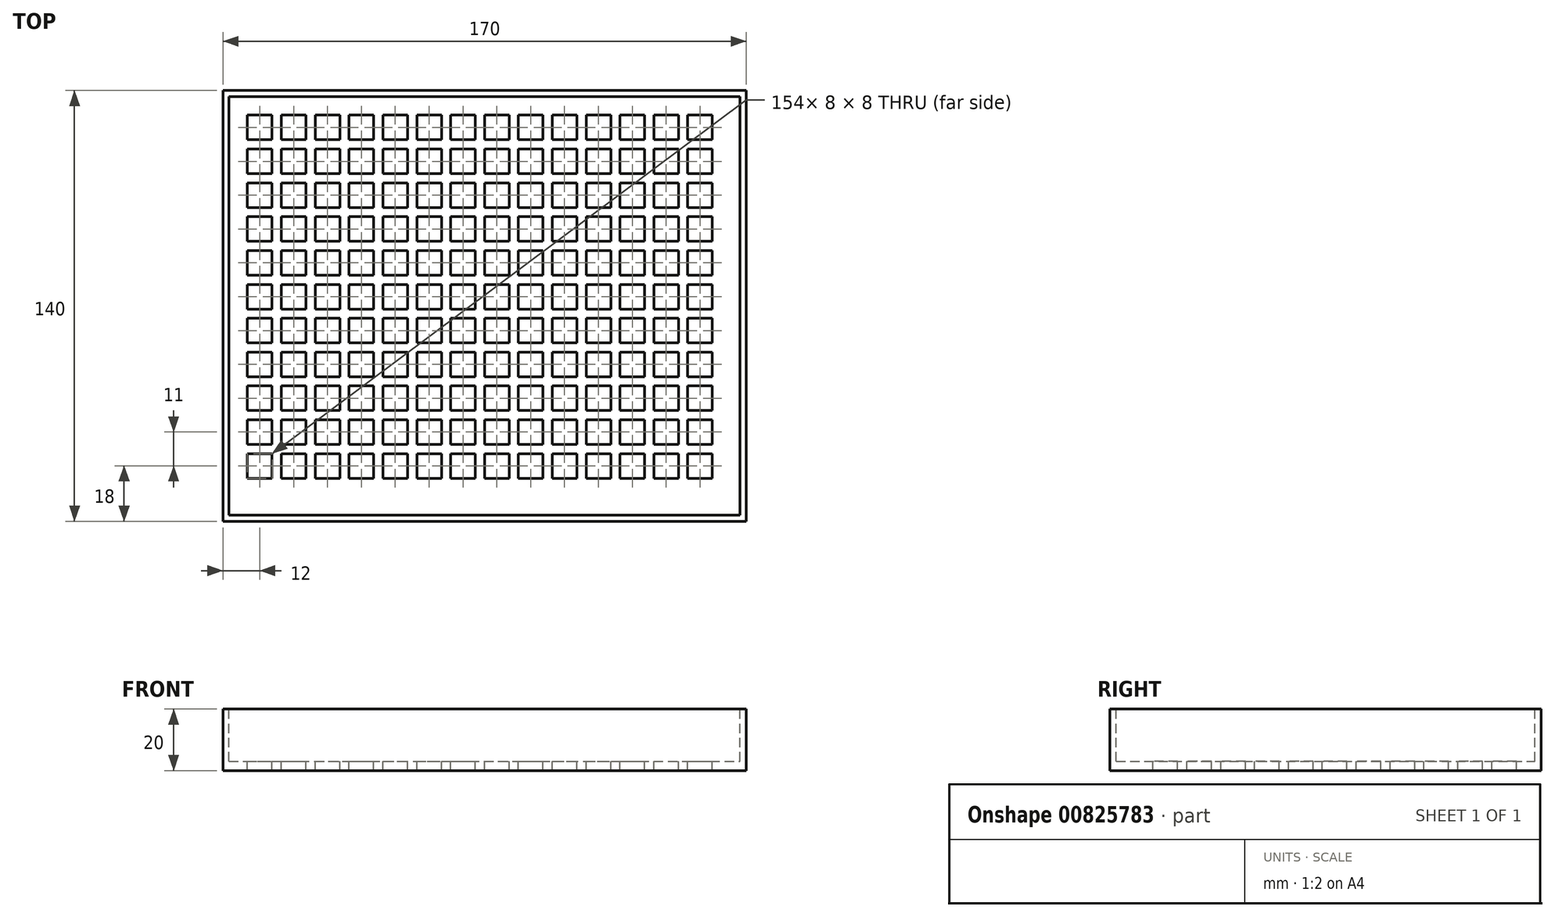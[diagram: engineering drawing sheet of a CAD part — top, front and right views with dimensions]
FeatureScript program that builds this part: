
annotation { "Feature Type Name" : "Feature", "Feature Type Description" : "" }
export const myFeature = defineFeature(function(context is Context, id is Id, definition is map)
    precondition{}
    {
        {
            var Q0;
            Q0=qCreatedBy(makeId("Top.planeOp"),FACE);
            var sketch = newSketch(context, id + "F0", { "sketchPlane" : qUnion([Q0])});
            skLineSegment(sketch, "E0.bottom", {"start": v(-85, 70) * mm, "end": v(85, 70) * mm});
            skLineSegment(sketch, "E0.top", {"start": v(-85, -70) * mm, "end": v(85, -70) * mm});
            skLineSegment(sketch, "E0.left", {"start": v(-85, 70) * mm, "end": v(-85, -70) * mm});
            skLineSegment(sketch, "E0.right", {"start": v(85, 70) * mm, "end": v(85, -70) * mm});
            skLineSegment(sketch, "E1", {"start": v(-85, 70) * mm, "end": v(85, -70) * mm, "construction": true});
            skLineSegment(sketch, "E2", {"start": v(85, 70) * mm, "end": v(-85, -70) * mm, "construction": true});
            skPoint(sketch, "E3", {"position": v(0, 0) * mm});
            skSolve(sketch);
        }
        {
            var Q0;
            Q0 = qSketchRegion(id + "F0", true);
            extrude(context, id + "F1", {"entities" : qUnion([Q0]), "depth" : 20 * mm, "offsetDistance" : 25 * mm});
        }
        {
            var Q0;
            Q0=makeQuery(id+"F1.opExtrude","CAP_FACE",FACE,{"disambiguationData":[OSD([sQuery(id+"F0.wireOp",EDGE,"E0.bottom"),sQuery(id+"F0.wireOp",EDGE,"E0.top"),sQuery(id+"F0.wireOp",EDGE,"E0.left"),sQuery(id+"F0.wireOp",EDGE,"E0.right")])],"isStart":false});
            var sketch = newSketch(context, id + "F2", { "sketchPlane" : qUnion([Q0])});
            skLineSegment(sketch, "E4.bottom", {"start": v(-77, 68) * mm, "end": v(77, 68) * mm});
            skLineSegment(sketch, "E4.top", {"start": v(-77, -68) * mm, "end": v(77, -68) * mm});
            skLineSegment(sketch, "E4.left", {"start": v(-83, 62) * mm, "end": v(-83, -62) * mm});
            skLineSegment(sketch, "E4.right", {"start": v(83, 62) * mm, "end": v(83, -62) * mm});
            skPoint(sketch, "E5.visualSharp", {"position": v(-83, 68) * mm});
            skPoint(sketch, "E6.visualSharp", {"position": v(-83, -68) * mm});
            skPoint(sketch, "E7.visualSharp", {"position": v(83, 68) * mm});
            skPoint(sketch, "E8.visualSharp", {"position": v(83, -68) * mm});
            skLineSegment(sketch, "E9", {"start": v(-83, 62) * mm, "end": v(-83, 68) * mm});
            skLineSegment(sketch, "E10", {"start": v(-83, 68) * mm, "end": v(-77, 68) * mm});
            skLineSegment(sketch, "E11", {"start": v(77, 68) * mm, "end": v(83, 68) * mm});
            skLineSegment(sketch, "E12", {"start": v(83, 62) * mm, "end": v(83, 68) * mm});
            skLineSegment(sketch, "E13", {"start": v(77, -68) * mm, "end": v(83, -68) * mm});
            skLineSegment(sketch, "E14", {"start": v(83, -62) * mm, "end": v(83, -68) * mm});
            skLineSegment(sketch, "E15", {"start": v(-77, -68) * mm, "end": v(-83, -68) * mm});
            skLineSegment(sketch, "E16", {"start": v(-83, -62) * mm, "end": v(-83, -68) * mm});
            skSolve(sketch);
        }
        {
            var Q0;
            Q0 = qSketchRegion(id + "F2", true);
            extrude(context, id + "F3", {"entities" : qUnion([Q0]), "operationType" : NewBodyOperationType.REMOVE, "oppositeDirection" : true, "depth" : 17 * mm, "offsetDistance" : 25 * mm});
        }
        {
            var Q0;
            Q0=makeQuery(id+"F3.boolean.opBoolean","COPY",FACE,{"derivedFrom":makeQuery(id+"F3.opExtrude","CAP_FACE",FACE,{"disambiguationData":[OSD([sQuery(id+"F2.wireOp",EDGE,"E4.bottom"),sQuery(id+"F2.wireOp",EDGE,"E4.top"),sQuery(id+"F2.wireOp",EDGE,"E4.left"),sQuery(id+"F2.wireOp",EDGE,"E4.right"),sQuery(id+"F2.wireOp",EDGE,"E5.filletArc"),sQuery(id+"F2.wireOp",EDGE,"E6.filletArc"),sQuery(id+"F2.wireOp",EDGE,"E7.filletArc"),sQuery(id+"F2.wireOp",EDGE,"E8.filletArc")])],"isStart":false})});
            var sketch = newSketch(context, id + "F4", { "sketchPlane" : qUnion([Q0])});
            skLineSegment(sketch, "E17.bottom", {"start": v(-77, 62) * mm, "end": v(-69, 62) * mm});
            skLineSegment(sketch, "E17.top", {"start": v(-77, 54) * mm, "end": v(-69, 54) * mm});
            skLineSegment(sketch, "E17.left", {"start": v(-77, 62) * mm, "end": v(-77, 54) * mm});
            skLineSegment(sketch, "E17.right", {"start": v(-69, 62) * mm, "end": v(-69, 54) * mm});
            skLineSegment(sketch, "E18.0.1.0", {"start": v(-69, 51) * mm, "end": v(-69, 43) * mm});
            skLineSegment(sketch, "E18.0.1.1", {"start": v(-77, 51) * mm, "end": v(-69, 51) * mm});
            skLineSegment(sketch, "E18.0.1.2", {"start": v(-77, 43) * mm, "end": v(-69, 43) * mm});
            skLineSegment(sketch, "E18.0.1.3", {"start": v(-77, 51) * mm, "end": v(-77, 43) * mm});
            skLineSegment(sketch, "E18.0.2.0", {"start": v(-69, 40) * mm, "end": v(-69, 32) * mm});
            skLineSegment(sketch, "E18.0.2.1", {"start": v(-77, 40) * mm, "end": v(-69, 40) * mm});
            skLineSegment(sketch, "E18.0.2.2", {"start": v(-77, 32) * mm, "end": v(-69, 32) * mm});
            skLineSegment(sketch, "E18.0.2.3", {"start": v(-77, 40) * mm, "end": v(-77, 32) * mm});
            skLineSegment(sketch, "E18.0.3.0", {"start": v(-69, 29) * mm, "end": v(-69, 21) * mm});
            skLineSegment(sketch, "E18.0.3.1", {"start": v(-77, 29) * mm, "end": v(-69, 29) * mm});
            skLineSegment(sketch, "E18.0.3.2", {"start": v(-77, 21) * mm, "end": v(-69, 21) * mm});
            skLineSegment(sketch, "E18.0.3.3", {"start": v(-77, 29) * mm, "end": v(-77, 21) * mm});
            skLineSegment(sketch, "E18.0.4.0", {"start": v(-69, 18) * mm, "end": v(-69, 10) * mm});
            skLineSegment(sketch, "E18.0.4.1", {"start": v(-77, 18) * mm, "end": v(-69, 18) * mm});
            skLineSegment(sketch, "E18.0.4.2", {"start": v(-77, 10) * mm, "end": v(-69, 10) * mm});
            skLineSegment(sketch, "E18.0.4.3", {"start": v(-77, 18) * mm, "end": v(-77, 10) * mm});
            skLineSegment(sketch, "E18.0.5.0", {"start": v(-69, 7) * mm, "end": v(-69, -1) * mm});
            skLineSegment(sketch, "E18.0.5.1", {"start": v(-77, 7) * mm, "end": v(-69, 7) * mm});
            skLineSegment(sketch, "E18.0.5.2", {"start": v(-77, -1) * mm, "end": v(-69, -1) * mm});
            skLineSegment(sketch, "E18.0.5.3", {"start": v(-77, 7) * mm, "end": v(-77, -1) * mm});
            skLineSegment(sketch, "E18.0.6.0", {"start": v(-69, -4) * mm, "end": v(-69, -12) * mm});
            skLineSegment(sketch, "E18.0.6.1", {"start": v(-77, -4) * mm, "end": v(-69, -4) * mm});
            skLineSegment(sketch, "E18.0.6.2", {"start": v(-77, -12) * mm, "end": v(-69, -12) * mm});
            skLineSegment(sketch, "E18.0.6.3", {"start": v(-77, -4) * mm, "end": v(-77, -12) * mm});
            skLineSegment(sketch, "E18.0.7.0", {"start": v(-69, -15) * mm, "end": v(-69, -23) * mm});
            skLineSegment(sketch, "E18.0.7.1", {"start": v(-77, -15) * mm, "end": v(-69, -15) * mm});
            skLineSegment(sketch, "E18.0.7.2", {"start": v(-77, -23) * mm, "end": v(-69, -23) * mm});
            skLineSegment(sketch, "E18.0.7.3", {"start": v(-77, -15) * mm, "end": v(-77, -23) * mm});
            skLineSegment(sketch, "E18.0.8.0", {"start": v(-69, -26) * mm, "end": v(-69, -34) * mm});
            skLineSegment(sketch, "E18.0.8.1", {"start": v(-77, -26) * mm, "end": v(-69, -26) * mm});
            skLineSegment(sketch, "E18.0.8.2", {"start": v(-77, -34) * mm, "end": v(-69, -34) * mm});
            skLineSegment(sketch, "E18.0.8.3", {"start": v(-77, -26) * mm, "end": v(-77, -34) * mm});
            skLineSegment(sketch, "E18.0.9.0", {"start": v(-69, -37) * mm, "end": v(-69, -45) * mm});
            skLineSegment(sketch, "E18.0.9.1", {"start": v(-77, -37) * mm, "end": v(-69, -37) * mm});
            skLineSegment(sketch, "E18.0.9.2", {"start": v(-77, -45) * mm, "end": v(-69, -45) * mm});
            skLineSegment(sketch, "E18.0.9.3", {"start": v(-77, -37) * mm, "end": v(-77, -45) * mm});
            skLineSegment(sketch, "E18.0.10.0", {"start": v(-69, -48) * mm, "end": v(-69, -56) * mm});
            skLineSegment(sketch, "E18.0.10.1", {"start": v(-77, -48) * mm, "end": v(-69, -48) * mm});
            skLineSegment(sketch, "E18.0.10.2", {"start": v(-77, -56) * mm, "end": v(-69, -56) * mm});
            skLineSegment(sketch, "E18.0.10.3", {"start": v(-77, -48) * mm, "end": v(-77, -56) * mm});
            skLineSegment(sketch, "E18.1.0.0", {"start": v(-58, 62) * mm, "end": v(-58, 54) * mm});
            skLineSegment(sketch, "E18.1.0.1", {"start": v(-66, 62) * mm, "end": v(-58, 62) * mm});
            skLineSegment(sketch, "E18.1.0.2", {"start": v(-66, 54) * mm, "end": v(-58, 54) * mm});
            skLineSegment(sketch, "E18.1.0.3", {"start": v(-66, 62) * mm, "end": v(-66, 54) * mm});
            skLineSegment(sketch, "E18.1.1.0", {"start": v(-58, 51) * mm, "end": v(-58, 43) * mm});
            skLineSegment(sketch, "E18.1.1.1", {"start": v(-66, 51) * mm, "end": v(-58, 51) * mm});
            skLineSegment(sketch, "E18.1.1.2", {"start": v(-66, 43) * mm, "end": v(-58, 43) * mm});
            skLineSegment(sketch, "E18.1.1.3", {"start": v(-66, 51) * mm, "end": v(-66, 43) * mm});
            skLineSegment(sketch, "E18.1.2.0", {"start": v(-58, 40) * mm, "end": v(-58, 32) * mm});
            skLineSegment(sketch, "E18.1.2.1", {"start": v(-66, 40) * mm, "end": v(-58, 40) * mm});
            skLineSegment(sketch, "E18.1.2.2", {"start": v(-66, 32) * mm, "end": v(-58, 32) * mm});
            skLineSegment(sketch, "E18.1.2.3", {"start": v(-66, 40) * mm, "end": v(-66, 32) * mm});
            skLineSegment(sketch, "E18.1.3.0", {"start": v(-58, 29) * mm, "end": v(-58, 21) * mm});
            skLineSegment(sketch, "E18.1.3.1", {"start": v(-66, 29) * mm, "end": v(-58, 29) * mm});
            skLineSegment(sketch, "E18.1.3.2", {"start": v(-66, 21) * mm, "end": v(-58, 21) * mm});
            skLineSegment(sketch, "E18.1.3.3", {"start": v(-66, 29) * mm, "end": v(-66, 21) * mm});
            skLineSegment(sketch, "E18.1.4.0", {"start": v(-58, 18) * mm, "end": v(-58, 10) * mm});
            skLineSegment(sketch, "E18.1.4.1", {"start": v(-66, 18) * mm, "end": v(-58, 18) * mm});
            skLineSegment(sketch, "E18.1.4.2", {"start": v(-66, 10) * mm, "end": v(-58, 10) * mm});
            skLineSegment(sketch, "E18.1.4.3", {"start": v(-66, 18) * mm, "end": v(-66, 10) * mm});
            skLineSegment(sketch, "E18.1.5.0", {"start": v(-58, 7) * mm, "end": v(-58, -1) * mm});
            skLineSegment(sketch, "E18.1.5.1", {"start": v(-66, 7) * mm, "end": v(-58, 7) * mm});
            skLineSegment(sketch, "E18.1.5.2", {"start": v(-66, -1) * mm, "end": v(-58, -1) * mm});
            skLineSegment(sketch, "E18.1.5.3", {"start": v(-66, 7) * mm, "end": v(-66, -1) * mm});
            skLineSegment(sketch, "E18.1.6.0", {"start": v(-58, -4) * mm, "end": v(-58, -12) * mm});
            skLineSegment(sketch, "E18.1.6.1", {"start": v(-66, -4) * mm, "end": v(-58, -4) * mm});
            skLineSegment(sketch, "E18.1.6.2", {"start": v(-66, -12) * mm, "end": v(-58, -12) * mm});
            skLineSegment(sketch, "E18.1.6.3", {"start": v(-66, -4) * mm, "end": v(-66, -12) * mm});
            skLineSegment(sketch, "E18.1.7.0", {"start": v(-58, -15) * mm, "end": v(-58, -23) * mm});
            skLineSegment(sketch, "E18.1.7.1", {"start": v(-66, -15) * mm, "end": v(-58, -15) * mm});
            skLineSegment(sketch, "E18.1.7.2", {"start": v(-66, -23) * mm, "end": v(-58, -23) * mm});
            skLineSegment(sketch, "E18.1.7.3", {"start": v(-66, -15) * mm, "end": v(-66, -23) * mm});
            skLineSegment(sketch, "E18.1.8.0", {"start": v(-58, -26) * mm, "end": v(-58, -34) * mm});
            skLineSegment(sketch, "E18.1.8.1", {"start": v(-66, -26) * mm, "end": v(-58, -26) * mm});
            skLineSegment(sketch, "E18.1.8.2", {"start": v(-66, -34) * mm, "end": v(-58, -34) * mm});
            skLineSegment(sketch, "E18.1.8.3", {"start": v(-66, -26) * mm, "end": v(-66, -34) * mm});
            skLineSegment(sketch, "E18.1.9.0", {"start": v(-58, -37) * mm, "end": v(-58, -45) * mm});
            skLineSegment(sketch, "E18.1.9.1", {"start": v(-66, -37) * mm, "end": v(-58, -37) * mm});
            skLineSegment(sketch, "E18.1.9.2", {"start": v(-66, -45) * mm, "end": v(-58, -45) * mm});
            skLineSegment(sketch, "E18.1.9.3", {"start": v(-66, -37) * mm, "end": v(-66, -45) * mm});
            skLineSegment(sketch, "E18.1.10.0", {"start": v(-58, -48) * mm, "end": v(-58, -56) * mm});
            skLineSegment(sketch, "E18.1.10.1", {"start": v(-66, -48) * mm, "end": v(-58, -48) * mm});
            skLineSegment(sketch, "E18.1.10.2", {"start": v(-66, -56) * mm, "end": v(-58, -56) * mm});
            skLineSegment(sketch, "E18.1.10.3", {"start": v(-66, -48) * mm, "end": v(-66, -56) * mm});
            skLineSegment(sketch, "E18.2.0.0", {"start": v(-47, 62) * mm, "end": v(-47, 54) * mm});
            skLineSegment(sketch, "E18.2.0.1", {"start": v(-55, 62) * mm, "end": v(-47, 62) * mm});
            skLineSegment(sketch, "E18.2.0.2", {"start": v(-55, 54) * mm, "end": v(-47, 54) * mm});
            skLineSegment(sketch, "E18.2.0.3", {"start": v(-55, 62) * mm, "end": v(-55, 54) * mm});
            skLineSegment(sketch, "E18.2.1.0", {"start": v(-47, 51) * mm, "end": v(-47, 43) * mm});
            skLineSegment(sketch, "E18.2.1.1", {"start": v(-55, 51) * mm, "end": v(-47, 51) * mm});
            skLineSegment(sketch, "E18.2.1.2", {"start": v(-55, 43) * mm, "end": v(-47, 43) * mm});
            skLineSegment(sketch, "E18.2.1.3", {"start": v(-55, 51) * mm, "end": v(-55, 43) * mm});
            skLineSegment(sketch, "E18.2.2.0", {"start": v(-47, 40) * mm, "end": v(-47, 32) * mm});
            skLineSegment(sketch, "E18.2.2.1", {"start": v(-55, 40) * mm, "end": v(-47, 40) * mm});
            skLineSegment(sketch, "E18.2.2.2", {"start": v(-55, 32) * mm, "end": v(-47, 32) * mm});
            skLineSegment(sketch, "E18.2.2.3", {"start": v(-55, 40) * mm, "end": v(-55, 32) * mm});
            skLineSegment(sketch, "E18.2.3.0", {"start": v(-47, 29) * mm, "end": v(-47, 21) * mm});
            skLineSegment(sketch, "E18.2.3.1", {"start": v(-55, 29) * mm, "end": v(-47, 29) * mm});
            skLineSegment(sketch, "E18.2.3.2", {"start": v(-55, 21) * mm, "end": v(-47, 21) * mm});
            skLineSegment(sketch, "E18.2.3.3", {"start": v(-55, 29) * mm, "end": v(-55, 21) * mm});
            skLineSegment(sketch, "E18.2.4.0", {"start": v(-47, 18) * mm, "end": v(-47, 10) * mm});
            skLineSegment(sketch, "E18.2.4.1", {"start": v(-55, 18) * mm, "end": v(-47, 18) * mm});
            skLineSegment(sketch, "E18.2.4.2", {"start": v(-55, 10) * mm, "end": v(-47, 10) * mm});
            skLineSegment(sketch, "E18.2.4.3", {"start": v(-55, 18) * mm, "end": v(-55, 10) * mm});
            skLineSegment(sketch, "E18.2.5.0", {"start": v(-47, 7) * mm, "end": v(-47, -1) * mm});
            skLineSegment(sketch, "E18.2.5.1", {"start": v(-55, 7) * mm, "end": v(-47, 7) * mm});
            skLineSegment(sketch, "E18.2.5.2", {"start": v(-55, -1) * mm, "end": v(-47, -1) * mm});
            skLineSegment(sketch, "E18.2.5.3", {"start": v(-55, 7) * mm, "end": v(-55, -1) * mm});
            skLineSegment(sketch, "E18.2.6.0", {"start": v(-47, -4) * mm, "end": v(-47, -12) * mm});
            skLineSegment(sketch, "E18.2.6.1", {"start": v(-55, -4) * mm, "end": v(-47, -4) * mm});
            skLineSegment(sketch, "E18.2.6.2", {"start": v(-55, -12) * mm, "end": v(-47, -12) * mm});
            skLineSegment(sketch, "E18.2.6.3", {"start": v(-55, -4) * mm, "end": v(-55, -12) * mm});
            skLineSegment(sketch, "E18.2.7.0", {"start": v(-47, -15) * mm, "end": v(-47, -23) * mm});
            skLineSegment(sketch, "E18.2.7.1", {"start": v(-55, -15) * mm, "end": v(-47, -15) * mm});
            skLineSegment(sketch, "E18.2.7.2", {"start": v(-55, -23) * mm, "end": v(-47, -23) * mm});
            skLineSegment(sketch, "E18.2.7.3", {"start": v(-55, -15) * mm, "end": v(-55, -23) * mm});
            skLineSegment(sketch, "E18.2.8.0", {"start": v(-47, -26) * mm, "end": v(-47, -34) * mm});
            skLineSegment(sketch, "E18.2.8.1", {"start": v(-55, -26) * mm, "end": v(-47, -26) * mm});
            skLineSegment(sketch, "E18.2.8.2", {"start": v(-55, -34) * mm, "end": v(-47, -34) * mm});
            skLineSegment(sketch, "E18.2.8.3", {"start": v(-55, -26) * mm, "end": v(-55, -34) * mm});
            skLineSegment(sketch, "E18.2.9.0", {"start": v(-47, -37) * mm, "end": v(-47, -45) * mm});
            skLineSegment(sketch, "E18.2.9.1", {"start": v(-55, -37) * mm, "end": v(-47, -37) * mm});
            skLineSegment(sketch, "E18.2.9.2", {"start": v(-55, -45) * mm, "end": v(-47, -45) * mm});
            skLineSegment(sketch, "E18.2.9.3", {"start": v(-55, -37) * mm, "end": v(-55, -45) * mm});
            skLineSegment(sketch, "E18.2.10.0", {"start": v(-47, -48) * mm, "end": v(-47, -56) * mm});
            skLineSegment(sketch, "E18.2.10.1", {"start": v(-55, -48) * mm, "end": v(-47, -48) * mm});
            skLineSegment(sketch, "E18.2.10.2", {"start": v(-55, -56) * mm, "end": v(-47, -56) * mm});
            skLineSegment(sketch, "E18.2.10.3", {"start": v(-55, -48) * mm, "end": v(-55, -56) * mm});
            skLineSegment(sketch, "E18.3.0.0", {"start": v(-36, 62) * mm, "end": v(-36, 54) * mm});
            skLineSegment(sketch, "E18.3.0.1", {"start": v(-44, 62) * mm, "end": v(-36, 62) * mm});
            skLineSegment(sketch, "E18.3.0.2", {"start": v(-44, 54) * mm, "end": v(-36, 54) * mm});
            skLineSegment(sketch, "E18.3.0.3", {"start": v(-44, 62) * mm, "end": v(-44, 54) * mm});
            skLineSegment(sketch, "E18.3.1.0", {"start": v(-36, 51) * mm, "end": v(-36, 43) * mm});
            skLineSegment(sketch, "E18.3.1.1", {"start": v(-44, 51) * mm, "end": v(-36, 51) * mm});
            skLineSegment(sketch, "E18.3.1.2", {"start": v(-44, 43) * mm, "end": v(-36, 43) * mm});
            skLineSegment(sketch, "E18.3.1.3", {"start": v(-44, 51) * mm, "end": v(-44, 43) * mm});
            skLineSegment(sketch, "E18.3.2.0", {"start": v(-36, 40) * mm, "end": v(-36, 32) * mm});
            skLineSegment(sketch, "E18.3.2.1", {"start": v(-44, 40) * mm, "end": v(-36, 40) * mm});
            skLineSegment(sketch, "E18.3.2.2", {"start": v(-44, 32) * mm, "end": v(-36, 32) * mm});
            skLineSegment(sketch, "E18.3.2.3", {"start": v(-44, 40) * mm, "end": v(-44, 32) * mm});
            skLineSegment(sketch, "E18.3.3.0", {"start": v(-36, 29) * mm, "end": v(-36, 21) * mm});
            skLineSegment(sketch, "E18.3.3.1", {"start": v(-44, 29) * mm, "end": v(-36, 29) * mm});
            skLineSegment(sketch, "E18.3.3.2", {"start": v(-44, 21) * mm, "end": v(-36, 21) * mm});
            skLineSegment(sketch, "E18.3.3.3", {"start": v(-44, 29) * mm, "end": v(-44, 21) * mm});
            skLineSegment(sketch, "E18.3.4.0", {"start": v(-36, 18) * mm, "end": v(-36, 10) * mm});
            skLineSegment(sketch, "E18.3.4.1", {"start": v(-44, 18) * mm, "end": v(-36, 18) * mm});
            skLineSegment(sketch, "E18.3.4.2", {"start": v(-44, 10) * mm, "end": v(-36, 10) * mm});
            skLineSegment(sketch, "E18.3.4.3", {"start": v(-44, 18) * mm, "end": v(-44, 10) * mm});
            skLineSegment(sketch, "E18.3.5.0", {"start": v(-36, 7) * mm, "end": v(-36, -1) * mm});
            skLineSegment(sketch, "E18.3.5.1", {"start": v(-44, 7) * mm, "end": v(-36, 7) * mm});
            skLineSegment(sketch, "E18.3.5.2", {"start": v(-44, -1) * mm, "end": v(-36, -1) * mm});
            skLineSegment(sketch, "E18.3.5.3", {"start": v(-44, 7) * mm, "end": v(-44, -1) * mm});
            skLineSegment(sketch, "E18.3.6.0", {"start": v(-36, -4) * mm, "end": v(-36, -12) * mm});
            skLineSegment(sketch, "E18.3.6.1", {"start": v(-44, -4) * mm, "end": v(-36, -4) * mm});
            skLineSegment(sketch, "E18.3.6.2", {"start": v(-44, -12) * mm, "end": v(-36, -12) * mm});
            skLineSegment(sketch, "E18.3.6.3", {"start": v(-44, -4) * mm, "end": v(-44, -12) * mm});
            skLineSegment(sketch, "E18.3.7.0", {"start": v(-36, -15) * mm, "end": v(-36, -23) * mm});
            skLineSegment(sketch, "E18.3.7.1", {"start": v(-44, -15) * mm, "end": v(-36, -15) * mm});
            skLineSegment(sketch, "E18.3.7.2", {"start": v(-44, -23) * mm, "end": v(-36, -23) * mm});
            skLineSegment(sketch, "E18.3.7.3", {"start": v(-44, -15) * mm, "end": v(-44, -23) * mm});
            skLineSegment(sketch, "E18.3.8.0", {"start": v(-36, -26) * mm, "end": v(-36, -34) * mm});
            skLineSegment(sketch, "E18.3.8.1", {"start": v(-44, -26) * mm, "end": v(-36, -26) * mm});
            skLineSegment(sketch, "E18.3.8.2", {"start": v(-44, -34) * mm, "end": v(-36, -34) * mm});
            skLineSegment(sketch, "E18.3.8.3", {"start": v(-44, -26) * mm, "end": v(-44, -34) * mm});
            skLineSegment(sketch, "E18.3.9.0", {"start": v(-36, -37) * mm, "end": v(-36, -45) * mm});
            skLineSegment(sketch, "E18.3.9.1", {"start": v(-44, -37) * mm, "end": v(-36, -37) * mm});
            skLineSegment(sketch, "E18.3.9.2", {"start": v(-44, -45) * mm, "end": v(-36, -45) * mm});
            skLineSegment(sketch, "E18.3.9.3", {"start": v(-44, -37) * mm, "end": v(-44, -45) * mm});
            skLineSegment(sketch, "E18.3.10.0", {"start": v(-36, -48) * mm, "end": v(-36, -56) * mm});
            skLineSegment(sketch, "E18.3.10.1", {"start": v(-44, -48) * mm, "end": v(-36, -48) * mm});
            skLineSegment(sketch, "E18.3.10.2", {"start": v(-44, -56) * mm, "end": v(-36, -56) * mm});
            skLineSegment(sketch, "E18.3.10.3", {"start": v(-44, -48) * mm, "end": v(-44, -56) * mm});
            skLineSegment(sketch, "E18.4.0.0", {"start": v(-25, 62) * mm, "end": v(-25, 54) * mm});
            skLineSegment(sketch, "E18.4.0.1", {"start": v(-33, 62) * mm, "end": v(-25, 62) * mm});
            skLineSegment(sketch, "E18.4.0.2", {"start": v(-33, 54) * mm, "end": v(-25, 54) * mm});
            skLineSegment(sketch, "E18.4.0.3", {"start": v(-33, 62) * mm, "end": v(-33, 54) * mm});
            skLineSegment(sketch, "E18.4.1.0", {"start": v(-25, 51) * mm, "end": v(-25, 43) * mm});
            skLineSegment(sketch, "E18.4.1.1", {"start": v(-33, 51) * mm, "end": v(-25, 51) * mm});
            skLineSegment(sketch, "E18.4.1.2", {"start": v(-33, 43) * mm, "end": v(-25, 43) * mm});
            skLineSegment(sketch, "E18.4.1.3", {"start": v(-33, 51) * mm, "end": v(-33, 43) * mm});
            skLineSegment(sketch, "E18.4.2.0", {"start": v(-25, 40) * mm, "end": v(-25, 32) * mm});
            skLineSegment(sketch, "E18.4.2.1", {"start": v(-33, 40) * mm, "end": v(-25, 40) * mm});
            skLineSegment(sketch, "E18.4.2.2", {"start": v(-33, 32) * mm, "end": v(-25, 32) * mm});
            skLineSegment(sketch, "E18.4.2.3", {"start": v(-33, 40) * mm, "end": v(-33, 32) * mm});
            skLineSegment(sketch, "E18.4.3.0", {"start": v(-25, 29) * mm, "end": v(-25, 21) * mm});
            skLineSegment(sketch, "E18.4.3.1", {"start": v(-33, 29) * mm, "end": v(-25, 29) * mm});
            skLineSegment(sketch, "E18.4.3.2", {"start": v(-33, 21) * mm, "end": v(-25, 21) * mm});
            skLineSegment(sketch, "E18.4.3.3", {"start": v(-33, 29) * mm, "end": v(-33, 21) * mm});
            skLineSegment(sketch, "E18.4.4.0", {"start": v(-25, 18) * mm, "end": v(-25, 10) * mm});
            skLineSegment(sketch, "E18.4.4.1", {"start": v(-33, 18) * mm, "end": v(-25, 18) * mm});
            skLineSegment(sketch, "E18.4.4.2", {"start": v(-33, 10) * mm, "end": v(-25, 10) * mm});
            skLineSegment(sketch, "E18.4.4.3", {"start": v(-33, 18) * mm, "end": v(-33, 10) * mm});
            skLineSegment(sketch, "E18.4.5.0", {"start": v(-25, 7) * mm, "end": v(-25, -1) * mm});
            skLineSegment(sketch, "E18.4.5.1", {"start": v(-33, 7) * mm, "end": v(-25, 7) * mm});
            skLineSegment(sketch, "E18.4.5.2", {"start": v(-33, -1) * mm, "end": v(-25, -1) * mm});
            skLineSegment(sketch, "E18.4.5.3", {"start": v(-33, 7) * mm, "end": v(-33, -1) * mm});
            skLineSegment(sketch, "E18.4.6.0", {"start": v(-25, -4) * mm, "end": v(-25, -12) * mm});
            skLineSegment(sketch, "E18.4.6.1", {"start": v(-33, -4) * mm, "end": v(-25, -4) * mm});
            skLineSegment(sketch, "E18.4.6.2", {"start": v(-33, -12) * mm, "end": v(-25, -12) * mm});
            skLineSegment(sketch, "E18.4.6.3", {"start": v(-33, -4) * mm, "end": v(-33, -12) * mm});
            skLineSegment(sketch, "E18.4.7.0", {"start": v(-25, -15) * mm, "end": v(-25, -23) * mm});
            skLineSegment(sketch, "E18.4.7.1", {"start": v(-33, -15) * mm, "end": v(-25, -15) * mm});
            skLineSegment(sketch, "E18.4.7.2", {"start": v(-33, -23) * mm, "end": v(-25, -23) * mm});
            skLineSegment(sketch, "E18.4.7.3", {"start": v(-33, -15) * mm, "end": v(-33, -23) * mm});
            skLineSegment(sketch, "E18.4.8.0", {"start": v(-25, -26) * mm, "end": v(-25, -34) * mm});
            skLineSegment(sketch, "E18.4.8.1", {"start": v(-33, -26) * mm, "end": v(-25, -26) * mm});
            skLineSegment(sketch, "E18.4.8.2", {"start": v(-33, -34) * mm, "end": v(-25, -34) * mm});
            skLineSegment(sketch, "E18.4.8.3", {"start": v(-33, -26) * mm, "end": v(-33, -34) * mm});
            skLineSegment(sketch, "E18.4.9.0", {"start": v(-25, -37) * mm, "end": v(-25, -45) * mm});
            skLineSegment(sketch, "E18.4.9.1", {"start": v(-33, -37) * mm, "end": v(-25, -37) * mm});
            skLineSegment(sketch, "E18.4.9.2", {"start": v(-33, -45) * mm, "end": v(-25, -45) * mm});
            skLineSegment(sketch, "E18.4.9.3", {"start": v(-33, -37) * mm, "end": v(-33, -45) * mm});
            skLineSegment(sketch, "E18.4.10.0", {"start": v(-25, -48) * mm, "end": v(-25, -56) * mm});
            skLineSegment(sketch, "E18.4.10.1", {"start": v(-33, -48) * mm, "end": v(-25, -48) * mm});
            skLineSegment(sketch, "E18.4.10.2", {"start": v(-33, -56) * mm, "end": v(-25, -56) * mm});
            skLineSegment(sketch, "E18.4.10.3", {"start": v(-33, -48) * mm, "end": v(-33, -56) * mm});
            skLineSegment(sketch, "E18.5.0.0", {"start": v(-14, 62) * mm, "end": v(-14, 54) * mm});
            skLineSegment(sketch, "E18.5.0.1", {"start": v(-22, 62) * mm, "end": v(-14, 62) * mm});
            skLineSegment(sketch, "E18.5.0.2", {"start": v(-22, 54) * mm, "end": v(-14, 54) * mm});
            skLineSegment(sketch, "E18.5.0.3", {"start": v(-22, 62) * mm, "end": v(-22, 54) * mm});
            skLineSegment(sketch, "E18.5.1.0", {"start": v(-14, 51) * mm, "end": v(-14, 43) * mm});
            skLineSegment(sketch, "E18.5.1.1", {"start": v(-22, 51) * mm, "end": v(-14, 51) * mm});
            skLineSegment(sketch, "E18.5.1.2", {"start": v(-22, 43) * mm, "end": v(-14, 43) * mm});
            skLineSegment(sketch, "E18.5.1.3", {"start": v(-22, 51) * mm, "end": v(-22, 43) * mm});
            skLineSegment(sketch, "E18.5.2.0", {"start": v(-14, 40) * mm, "end": v(-14, 32) * mm});
            skLineSegment(sketch, "E18.5.2.1", {"start": v(-22, 40) * mm, "end": v(-14, 40) * mm});
            skLineSegment(sketch, "E18.5.2.2", {"start": v(-22, 32) * mm, "end": v(-14, 32) * mm});
            skLineSegment(sketch, "E18.5.2.3", {"start": v(-22, 40) * mm, "end": v(-22, 32) * mm});
            skLineSegment(sketch, "E18.5.3.0", {"start": v(-14, 29) * mm, "end": v(-14, 21) * mm});
            skLineSegment(sketch, "E18.5.3.1", {"start": v(-22, 29) * mm, "end": v(-14, 29) * mm});
            skLineSegment(sketch, "E18.5.3.2", {"start": v(-22, 21) * mm, "end": v(-14, 21) * mm});
            skLineSegment(sketch, "E18.5.3.3", {"start": v(-22, 29) * mm, "end": v(-22, 21) * mm});
            skLineSegment(sketch, "E18.5.4.0", {"start": v(-14, 18) * mm, "end": v(-14, 10) * mm});
            skLineSegment(sketch, "E18.5.4.1", {"start": v(-22, 18) * mm, "end": v(-14, 18) * mm});
            skLineSegment(sketch, "E18.5.4.2", {"start": v(-22, 10) * mm, "end": v(-14, 10) * mm});
            skLineSegment(sketch, "E18.5.4.3", {"start": v(-22, 18) * mm, "end": v(-22, 10) * mm});
            skLineSegment(sketch, "E18.5.5.0", {"start": v(-14, 7) * mm, "end": v(-14, -1) * mm});
            skLineSegment(sketch, "E18.5.5.1", {"start": v(-22, 7) * mm, "end": v(-14, 7) * mm});
            skLineSegment(sketch, "E18.5.5.2", {"start": v(-22, -1) * mm, "end": v(-14, -1) * mm});
            skLineSegment(sketch, "E18.5.5.3", {"start": v(-22, 7) * mm, "end": v(-22, -1) * mm});
            skLineSegment(sketch, "E18.5.6.0", {"start": v(-14, -4) * mm, "end": v(-14, -12) * mm});
            skLineSegment(sketch, "E18.5.6.1", {"start": v(-22, -4) * mm, "end": v(-14, -4) * mm});
            skLineSegment(sketch, "E18.5.6.2", {"start": v(-22, -12) * mm, "end": v(-14, -12) * mm});
            skLineSegment(sketch, "E18.5.6.3", {"start": v(-22, -4) * mm, "end": v(-22, -12) * mm});
            skLineSegment(sketch, "E18.5.7.0", {"start": v(-14, -15) * mm, "end": v(-14, -23) * mm});
            skLineSegment(sketch, "E18.5.7.1", {"start": v(-22, -15) * mm, "end": v(-14, -15) * mm});
            skLineSegment(sketch, "E18.5.7.2", {"start": v(-22, -23) * mm, "end": v(-14, -23) * mm});
            skLineSegment(sketch, "E18.5.7.3", {"start": v(-22, -15) * mm, "end": v(-22, -23) * mm});
            skLineSegment(sketch, "E18.5.8.0", {"start": v(-14, -26) * mm, "end": v(-14, -34) * mm});
            skLineSegment(sketch, "E18.5.8.1", {"start": v(-22, -26) * mm, "end": v(-14, -26) * mm});
            skLineSegment(sketch, "E18.5.8.2", {"start": v(-22, -34) * mm, "end": v(-14, -34) * mm});
            skLineSegment(sketch, "E18.5.8.3", {"start": v(-22, -26) * mm, "end": v(-22, -34) * mm});
            skLineSegment(sketch, "E18.5.9.0", {"start": v(-14, -37) * mm, "end": v(-14, -45) * mm});
            skLineSegment(sketch, "E18.5.9.1", {"start": v(-22, -37) * mm, "end": v(-14, -37) * mm});
            skLineSegment(sketch, "E18.5.9.2", {"start": v(-22, -45) * mm, "end": v(-14, -45) * mm});
            skLineSegment(sketch, "E18.5.9.3", {"start": v(-22, -37) * mm, "end": v(-22, -45) * mm});
            skLineSegment(sketch, "E18.5.10.0", {"start": v(-14, -48) * mm, "end": v(-14, -56) * mm});
            skLineSegment(sketch, "E18.5.10.1", {"start": v(-22, -48) * mm, "end": v(-14, -48) * mm});
            skLineSegment(sketch, "E18.5.10.2", {"start": v(-22, -56) * mm, "end": v(-14, -56) * mm});
            skLineSegment(sketch, "E18.5.10.3", {"start": v(-22, -48) * mm, "end": v(-22, -56) * mm});
            skLineSegment(sketch, "E18.6.0.0", {"start": v(-3, 62) * mm, "end": v(-3, 54) * mm});
            skLineSegment(sketch, "E18.6.0.1", {"start": v(-11, 62) * mm, "end": v(-3, 62) * mm});
            skLineSegment(sketch, "E18.6.0.2", {"start": v(-11, 54) * mm, "end": v(-3, 54) * mm});
            skLineSegment(sketch, "E18.6.0.3", {"start": v(-11, 62) * mm, "end": v(-11, 54) * mm});
            skLineSegment(sketch, "E18.6.1.0", {"start": v(-3, 51) * mm, "end": v(-3, 43) * mm});
            skLineSegment(sketch, "E18.6.1.1", {"start": v(-11, 51) * mm, "end": v(-3, 51) * mm});
            skLineSegment(sketch, "E18.6.1.2", {"start": v(-11, 43) * mm, "end": v(-3, 43) * mm});
            skLineSegment(sketch, "E18.6.1.3", {"start": v(-11, 51) * mm, "end": v(-11, 43) * mm});
            skLineSegment(sketch, "E18.6.2.0", {"start": v(-3, 40) * mm, "end": v(-3, 32) * mm});
            skLineSegment(sketch, "E18.6.2.1", {"start": v(-11, 40) * mm, "end": v(-3, 40) * mm});
            skLineSegment(sketch, "E18.6.2.2", {"start": v(-11, 32) * mm, "end": v(-3, 32) * mm});
            skLineSegment(sketch, "E18.6.2.3", {"start": v(-11, 40) * mm, "end": v(-11, 32) * mm});
            skLineSegment(sketch, "E18.6.3.0", {"start": v(-3, 29) * mm, "end": v(-3, 21) * mm});
            skLineSegment(sketch, "E18.6.3.1", {"start": v(-11, 29) * mm, "end": v(-3, 29) * mm});
            skLineSegment(sketch, "E18.6.3.2", {"start": v(-11, 21) * mm, "end": v(-3, 21) * mm});
            skLineSegment(sketch, "E18.6.3.3", {"start": v(-11, 29) * mm, "end": v(-11, 21) * mm});
            skLineSegment(sketch, "E18.6.4.0", {"start": v(-3, 18) * mm, "end": v(-3, 10) * mm});
            skLineSegment(sketch, "E18.6.4.1", {"start": v(-11, 18) * mm, "end": v(-3, 18) * mm});
            skLineSegment(sketch, "E18.6.4.2", {"start": v(-11, 10) * mm, "end": v(-3, 10) * mm});
            skLineSegment(sketch, "E18.6.4.3", {"start": v(-11, 18) * mm, "end": v(-11, 10) * mm});
            skLineSegment(sketch, "E18.6.5.0", {"start": v(-3, 7) * mm, "end": v(-3, -1) * mm});
            skLineSegment(sketch, "E18.6.5.1", {"start": v(-11, 7) * mm, "end": v(-3, 7) * mm});
            skLineSegment(sketch, "E18.6.5.2", {"start": v(-11, -1) * mm, "end": v(-3, -1) * mm});
            skLineSegment(sketch, "E18.6.5.3", {"start": v(-11, 7) * mm, "end": v(-11, -1) * mm});
            skLineSegment(sketch, "E18.6.6.0", {"start": v(-3, -4) * mm, "end": v(-3, -12) * mm});
            skLineSegment(sketch, "E18.6.6.1", {"start": v(-11, -4) * mm, "end": v(-3, -4) * mm});
            skLineSegment(sketch, "E18.6.6.2", {"start": v(-11, -12) * mm, "end": v(-3, -12) * mm});
            skLineSegment(sketch, "E18.6.6.3", {"start": v(-11, -4) * mm, "end": v(-11, -12) * mm});
            skLineSegment(sketch, "E18.6.7.0", {"start": v(-3, -15) * mm, "end": v(-3, -23) * mm});
            skLineSegment(sketch, "E18.6.7.1", {"start": v(-11, -15) * mm, "end": v(-3, -15) * mm});
            skLineSegment(sketch, "E18.6.7.2", {"start": v(-11, -23) * mm, "end": v(-3, -23) * mm});
            skLineSegment(sketch, "E18.6.7.3", {"start": v(-11, -15) * mm, "end": v(-11, -23) * mm});
            skLineSegment(sketch, "E18.6.8.0", {"start": v(-3, -26) * mm, "end": v(-3, -34) * mm});
            skLineSegment(sketch, "E18.6.8.1", {"start": v(-11, -26) * mm, "end": v(-3, -26) * mm});
            skLineSegment(sketch, "E18.6.8.2", {"start": v(-11, -34) * mm, "end": v(-3, -34) * mm});
            skLineSegment(sketch, "E18.6.8.3", {"start": v(-11, -26) * mm, "end": v(-11, -34) * mm});
            skLineSegment(sketch, "E18.6.9.0", {"start": v(-3, -37) * mm, "end": v(-3, -45) * mm});
            skLineSegment(sketch, "E18.6.9.1", {"start": v(-11, -37) * mm, "end": v(-3, -37) * mm});
            skLineSegment(sketch, "E18.6.9.2", {"start": v(-11, -45) * mm, "end": v(-3, -45) * mm});
            skLineSegment(sketch, "E18.6.9.3", {"start": v(-11, -37) * mm, "end": v(-11, -45) * mm});
            skLineSegment(sketch, "E18.6.10.0", {"start": v(-3, -48) * mm, "end": v(-3, -56) * mm});
            skLineSegment(sketch, "E18.6.10.1", {"start": v(-11, -48) * mm, "end": v(-3, -48) * mm});
            skLineSegment(sketch, "E18.6.10.2", {"start": v(-11, -56) * mm, "end": v(-3, -56) * mm});
            skLineSegment(sketch, "E18.6.10.3", {"start": v(-11, -48) * mm, "end": v(-11, -56) * mm});
            skLineSegment(sketch, "E18.7.0.0", {"start": v(8, 62) * mm, "end": v(8, 54) * mm});
            skLineSegment(sketch, "E18.7.0.1", {"start": v(0, 62) * mm, "end": v(8, 62) * mm});
            skLineSegment(sketch, "E18.7.0.2", {"start": v(0, 54) * mm, "end": v(8, 54) * mm});
            skLineSegment(sketch, "E18.7.0.3", {"start": v(0, 62) * mm, "end": v(0, 54) * mm});
            skLineSegment(sketch, "E18.7.1.0", {"start": v(8, 51) * mm, "end": v(8, 43) * mm});
            skLineSegment(sketch, "E18.7.1.1", {"start": v(0, 51) * mm, "end": v(8, 51) * mm});
            skLineSegment(sketch, "E18.7.1.2", {"start": v(0, 43) * mm, "end": v(8, 43) * mm});
            skLineSegment(sketch, "E18.7.1.3", {"start": v(0, 51) * mm, "end": v(0, 43) * mm});
            skLineSegment(sketch, "E18.7.2.0", {"start": v(8, 40) * mm, "end": v(8, 32) * mm});
            skLineSegment(sketch, "E18.7.2.1", {"start": v(0, 40) * mm, "end": v(8, 40) * mm});
            skLineSegment(sketch, "E18.7.2.2", {"start": v(0, 32) * mm, "end": v(8, 32) * mm});
            skLineSegment(sketch, "E18.7.2.3", {"start": v(0, 40) * mm, "end": v(0, 32) * mm});
            skLineSegment(sketch, "E18.7.3.0", {"start": v(8, 29) * mm, "end": v(8, 21) * mm});
            skLineSegment(sketch, "E18.7.3.1", {"start": v(0, 29) * mm, "end": v(8, 29) * mm});
            skLineSegment(sketch, "E18.7.3.2", {"start": v(0, 21) * mm, "end": v(8, 21) * mm});
            skLineSegment(sketch, "E18.7.3.3", {"start": v(0, 29) * mm, "end": v(0, 21) * mm});
            skLineSegment(sketch, "E18.7.4.0", {"start": v(8, 18) * mm, "end": v(8, 10) * mm});
            skLineSegment(sketch, "E18.7.4.1", {"start": v(0, 18) * mm, "end": v(8, 18) * mm});
            skLineSegment(sketch, "E18.7.4.2", {"start": v(0, 10) * mm, "end": v(8, 10) * mm});
            skLineSegment(sketch, "E18.7.4.3", {"start": v(0, 18) * mm, "end": v(0, 10) * mm});
            skLineSegment(sketch, "E18.7.5.0", {"start": v(8, 7) * mm, "end": v(8, -1) * mm});
            skLineSegment(sketch, "E18.7.5.1", {"start": v(0, 7) * mm, "end": v(8, 7) * mm});
            skLineSegment(sketch, "E18.7.5.2", {"start": v(0, -1) * mm, "end": v(8, -1) * mm});
            skLineSegment(sketch, "E18.7.5.3", {"start": v(0, 7) * mm, "end": v(0, -1) * mm});
            skLineSegment(sketch, "E18.7.6.0", {"start": v(8, -4) * mm, "end": v(8, -12) * mm});
            skLineSegment(sketch, "E18.7.6.1", {"start": v(0, -4) * mm, "end": v(8, -4) * mm});
            skLineSegment(sketch, "E18.7.6.2", {"start": v(0, -12) * mm, "end": v(8, -12) * mm});
            skLineSegment(sketch, "E18.7.6.3", {"start": v(0, -4) * mm, "end": v(0, -12) * mm});
            skLineSegment(sketch, "E18.7.7.0", {"start": v(8, -15) * mm, "end": v(8, -23) * mm});
            skLineSegment(sketch, "E18.7.7.1", {"start": v(0, -15) * mm, "end": v(8, -15) * mm});
            skLineSegment(sketch, "E18.7.7.2", {"start": v(0, -23) * mm, "end": v(8, -23) * mm});
            skLineSegment(sketch, "E18.7.7.3", {"start": v(0, -15) * mm, "end": v(0, -23) * mm});
            skLineSegment(sketch, "E18.7.8.0", {"start": v(8, -26) * mm, "end": v(8, -34) * mm});
            skLineSegment(sketch, "E18.7.8.1", {"start": v(0, -26) * mm, "end": v(8, -26) * mm});
            skLineSegment(sketch, "E18.7.8.2", {"start": v(0, -34) * mm, "end": v(8, -34) * mm});
            skLineSegment(sketch, "E18.7.8.3", {"start": v(0, -26) * mm, "end": v(0, -34) * mm});
            skLineSegment(sketch, "E18.7.9.0", {"start": v(8, -37) * mm, "end": v(8, -45) * mm});
            skLineSegment(sketch, "E18.7.9.1", {"start": v(0, -37) * mm, "end": v(8, -37) * mm});
            skLineSegment(sketch, "E18.7.9.2", {"start": v(0, -45) * mm, "end": v(8, -45) * mm});
            skLineSegment(sketch, "E18.7.9.3", {"start": v(0, -37) * mm, "end": v(0, -45) * mm});
            skLineSegment(sketch, "E18.7.10.0", {"start": v(8, -48) * mm, "end": v(8, -56) * mm});
            skLineSegment(sketch, "E18.7.10.1", {"start": v(0, -48) * mm, "end": v(8, -48) * mm});
            skLineSegment(sketch, "E18.7.10.2", {"start": v(0, -56) * mm, "end": v(8, -56) * mm});
            skLineSegment(sketch, "E18.7.10.3", {"start": v(0, -48) * mm, "end": v(0, -56) * mm});
            skLineSegment(sketch, "E18.8.0.0", {"start": v(19, 62) * mm, "end": v(19, 54) * mm});
            skLineSegment(sketch, "E18.8.0.1", {"start": v(11, 62) * mm, "end": v(19, 62) * mm});
            skLineSegment(sketch, "E18.8.0.2", {"start": v(11, 54) * mm, "end": v(19, 54) * mm});
            skLineSegment(sketch, "E18.8.0.3", {"start": v(11, 62) * mm, "end": v(11, 54) * mm});
            skLineSegment(sketch, "E18.8.1.0", {"start": v(19, 51) * mm, "end": v(19, 43) * mm});
            skLineSegment(sketch, "E18.8.1.1", {"start": v(11, 51) * mm, "end": v(19, 51) * mm});
            skLineSegment(sketch, "E18.8.1.2", {"start": v(11, 43) * mm, "end": v(19, 43) * mm});
            skLineSegment(sketch, "E18.8.1.3", {"start": v(11, 51) * mm, "end": v(11, 43) * mm});
            skLineSegment(sketch, "E18.8.2.0", {"start": v(19, 40) * mm, "end": v(19, 32) * mm});
            skLineSegment(sketch, "E18.8.2.1", {"start": v(11, 40) * mm, "end": v(19, 40) * mm});
            skLineSegment(sketch, "E18.8.2.2", {"start": v(11, 32) * mm, "end": v(19, 32) * mm});
            skLineSegment(sketch, "E18.8.2.3", {"start": v(11, 40) * mm, "end": v(11, 32) * mm});
            skLineSegment(sketch, "E18.8.3.0", {"start": v(19, 29) * mm, "end": v(19, 21) * mm});
            skLineSegment(sketch, "E18.8.3.1", {"start": v(11, 29) * mm, "end": v(19, 29) * mm});
            skLineSegment(sketch, "E18.8.3.2", {"start": v(11, 21) * mm, "end": v(19, 21) * mm});
            skLineSegment(sketch, "E18.8.3.3", {"start": v(11, 29) * mm, "end": v(11, 21) * mm});
            skLineSegment(sketch, "E18.8.4.0", {"start": v(19, 18) * mm, "end": v(19, 10) * mm});
            skLineSegment(sketch, "E18.8.4.1", {"start": v(11, 18) * mm, "end": v(19, 18) * mm});
            skLineSegment(sketch, "E18.8.4.2", {"start": v(11, 10) * mm, "end": v(19, 10) * mm});
            skLineSegment(sketch, "E18.8.4.3", {"start": v(11, 18) * mm, "end": v(11, 10) * mm});
            skLineSegment(sketch, "E18.8.5.0", {"start": v(19, 7) * mm, "end": v(19, -1) * mm});
            skLineSegment(sketch, "E18.8.5.1", {"start": v(11, 7) * mm, "end": v(19, 7) * mm});
            skLineSegment(sketch, "E18.8.5.2", {"start": v(11, -1) * mm, "end": v(19, -1) * mm});
            skLineSegment(sketch, "E18.8.5.3", {"start": v(11, 7) * mm, "end": v(11, -1) * mm});
            skLineSegment(sketch, "E18.8.6.0", {"start": v(19, -4) * mm, "end": v(19, -12) * mm});
            skLineSegment(sketch, "E18.8.6.1", {"start": v(11, -4) * mm, "end": v(19, -4) * mm});
            skLineSegment(sketch, "E18.8.6.2", {"start": v(11, -12) * mm, "end": v(19, -12) * mm});
            skLineSegment(sketch, "E18.8.6.3", {"start": v(11, -4) * mm, "end": v(11, -12) * mm});
            skLineSegment(sketch, "E18.8.7.0", {"start": v(19, -15) * mm, "end": v(19, -23) * mm});
            skLineSegment(sketch, "E18.8.7.1", {"start": v(11, -15) * mm, "end": v(19, -15) * mm});
            skLineSegment(sketch, "E18.8.7.2", {"start": v(11, -23) * mm, "end": v(19, -23) * mm});
            skLineSegment(sketch, "E18.8.7.3", {"start": v(11, -15) * mm, "end": v(11, -23) * mm});
            skLineSegment(sketch, "E18.8.8.0", {"start": v(19, -26) * mm, "end": v(19, -34) * mm});
            skLineSegment(sketch, "E18.8.8.1", {"start": v(11, -26) * mm, "end": v(19, -26) * mm});
            skLineSegment(sketch, "E18.8.8.2", {"start": v(11, -34) * mm, "end": v(19, -34) * mm});
            skLineSegment(sketch, "E18.8.8.3", {"start": v(11, -26) * mm, "end": v(11, -34) * mm});
            skLineSegment(sketch, "E18.8.9.0", {"start": v(19, -37) * mm, "end": v(19, -45) * mm});
            skLineSegment(sketch, "E18.8.9.1", {"start": v(11, -37) * mm, "end": v(19, -37) * mm});
            skLineSegment(sketch, "E18.8.9.2", {"start": v(11, -45) * mm, "end": v(19, -45) * mm});
            skLineSegment(sketch, "E18.8.9.3", {"start": v(11, -37) * mm, "end": v(11, -45) * mm});
            skLineSegment(sketch, "E18.8.10.0", {"start": v(19, -48) * mm, "end": v(19, -56) * mm});
            skLineSegment(sketch, "E18.8.10.1", {"start": v(11, -48) * mm, "end": v(19, -48) * mm});
            skLineSegment(sketch, "E18.8.10.2", {"start": v(11, -56) * mm, "end": v(19, -56) * mm});
            skLineSegment(sketch, "E18.8.10.3", {"start": v(11, -48) * mm, "end": v(11, -56) * mm});
            skLineSegment(sketch, "E18.9.0.0", {"start": v(30, 62) * mm, "end": v(30, 54) * mm});
            skLineSegment(sketch, "E18.9.0.1", {"start": v(22, 62) * mm, "end": v(30, 62) * mm});
            skLineSegment(sketch, "E18.9.0.2", {"start": v(22, 54) * mm, "end": v(30, 54) * mm});
            skLineSegment(sketch, "E18.9.0.3", {"start": v(22, 62) * mm, "end": v(22, 54) * mm});
            skLineSegment(sketch, "E18.9.1.0", {"start": v(30, 51) * mm, "end": v(30, 43) * mm});
            skLineSegment(sketch, "E18.9.1.1", {"start": v(22, 51) * mm, "end": v(30, 51) * mm});
            skLineSegment(sketch, "E18.9.1.2", {"start": v(22, 43) * mm, "end": v(30, 43) * mm});
            skLineSegment(sketch, "E18.9.1.3", {"start": v(22, 51) * mm, "end": v(22, 43) * mm});
            skLineSegment(sketch, "E18.9.2.0", {"start": v(30, 40) * mm, "end": v(30, 32) * mm});
            skLineSegment(sketch, "E18.9.2.1", {"start": v(22, 40) * mm, "end": v(30, 40) * mm});
            skLineSegment(sketch, "E18.9.2.2", {"start": v(22, 32) * mm, "end": v(30, 32) * mm});
            skLineSegment(sketch, "E18.9.2.3", {"start": v(22, 40) * mm, "end": v(22, 32) * mm});
            skLineSegment(sketch, "E18.9.3.0", {"start": v(30, 29) * mm, "end": v(30, 21) * mm});
            skLineSegment(sketch, "E18.9.3.1", {"start": v(22, 29) * mm, "end": v(30, 29) * mm});
            skLineSegment(sketch, "E18.9.3.2", {"start": v(22, 21) * mm, "end": v(30, 21) * mm});
            skLineSegment(sketch, "E18.9.3.3", {"start": v(22, 29) * mm, "end": v(22, 21) * mm});
            skLineSegment(sketch, "E18.9.4.0", {"start": v(30, 18) * mm, "end": v(30, 10) * mm});
            skLineSegment(sketch, "E18.9.4.1", {"start": v(22, 18) * mm, "end": v(30, 18) * mm});
            skLineSegment(sketch, "E18.9.4.2", {"start": v(22, 10) * mm, "end": v(30, 10) * mm});
            skLineSegment(sketch, "E18.9.4.3", {"start": v(22, 18) * mm, "end": v(22, 10) * mm});
            skLineSegment(sketch, "E18.9.5.0", {"start": v(30, 7) * mm, "end": v(30, -1) * mm});
            skLineSegment(sketch, "E18.9.5.1", {"start": v(22, 7) * mm, "end": v(30, 7) * mm});
            skLineSegment(sketch, "E18.9.5.2", {"start": v(22, -1) * mm, "end": v(30, -1) * mm});
            skLineSegment(sketch, "E18.9.5.3", {"start": v(22, 7) * mm, "end": v(22, -1) * mm});
            skLineSegment(sketch, "E18.9.6.0", {"start": v(30, -4) * mm, "end": v(30, -12) * mm});
            skLineSegment(sketch, "E18.9.6.1", {"start": v(22, -4) * mm, "end": v(30, -4) * mm});
            skLineSegment(sketch, "E18.9.6.2", {"start": v(22, -12) * mm, "end": v(30, -12) * mm});
            skLineSegment(sketch, "E18.9.6.3", {"start": v(22, -4) * mm, "end": v(22, -12) * mm});
            skLineSegment(sketch, "E18.9.7.0", {"start": v(30, -15) * mm, "end": v(30, -23) * mm});
            skLineSegment(sketch, "E18.9.7.1", {"start": v(22, -15) * mm, "end": v(30, -15) * mm});
            skLineSegment(sketch, "E18.9.7.2", {"start": v(22, -23) * mm, "end": v(30, -23) * mm});
            skLineSegment(sketch, "E18.9.7.3", {"start": v(22, -15) * mm, "end": v(22, -23) * mm});
            skLineSegment(sketch, "E18.9.8.0", {"start": v(30, -26) * mm, "end": v(30, -34) * mm});
            skLineSegment(sketch, "E18.9.8.1", {"start": v(22, -26) * mm, "end": v(30, -26) * mm});
            skLineSegment(sketch, "E18.9.8.2", {"start": v(22, -34) * mm, "end": v(30, -34) * mm});
            skLineSegment(sketch, "E18.9.8.3", {"start": v(22, -26) * mm, "end": v(22, -34) * mm});
            skLineSegment(sketch, "E18.9.9.0", {"start": v(30, -37) * mm, "end": v(30, -45) * mm});
            skLineSegment(sketch, "E18.9.9.1", {"start": v(22, -37) * mm, "end": v(30, -37) * mm});
            skLineSegment(sketch, "E18.9.9.2", {"start": v(22, -45) * mm, "end": v(30, -45) * mm});
            skLineSegment(sketch, "E18.9.9.3", {"start": v(22, -37) * mm, "end": v(22, -45) * mm});
            skLineSegment(sketch, "E18.9.10.0", {"start": v(30, -48) * mm, "end": v(30, -56) * mm});
            skLineSegment(sketch, "E18.9.10.1", {"start": v(22, -48) * mm, "end": v(30, -48) * mm});
            skLineSegment(sketch, "E18.9.10.2", {"start": v(22, -56) * mm, "end": v(30, -56) * mm});
            skLineSegment(sketch, "E18.9.10.3", {"start": v(22, -48) * mm, "end": v(22, -56) * mm});
            skLineSegment(sketch, "E18.10.0.0", {"start": v(41, 62) * mm, "end": v(41, 54) * mm});
            skLineSegment(sketch, "E18.10.0.1", {"start": v(33, 62) * mm, "end": v(41, 62) * mm});
            skLineSegment(sketch, "E18.10.0.2", {"start": v(33, 54) * mm, "end": v(41, 54) * mm});
            skLineSegment(sketch, "E18.10.0.3", {"start": v(33, 62) * mm, "end": v(33, 54) * mm});
            skLineSegment(sketch, "E18.10.1.0", {"start": v(41, 51) * mm, "end": v(41, 43) * mm});
            skLineSegment(sketch, "E18.10.1.1", {"start": v(33, 51) * mm, "end": v(41, 51) * mm});
            skLineSegment(sketch, "E18.10.1.2", {"start": v(33, 43) * mm, "end": v(41, 43) * mm});
            skLineSegment(sketch, "E18.10.1.3", {"start": v(33, 51) * mm, "end": v(33, 43) * mm});
            skLineSegment(sketch, "E18.10.2.0", {"start": v(41, 40) * mm, "end": v(41, 32) * mm});
            skLineSegment(sketch, "E18.10.2.1", {"start": v(33, 40) * mm, "end": v(41, 40) * mm});
            skLineSegment(sketch, "E18.10.2.2", {"start": v(33, 32) * mm, "end": v(41, 32) * mm});
            skLineSegment(sketch, "E18.10.2.3", {"start": v(33, 40) * mm, "end": v(33, 32) * mm});
            skLineSegment(sketch, "E18.10.3.0", {"start": v(41, 29) * mm, "end": v(41, 21) * mm});
            skLineSegment(sketch, "E18.10.3.1", {"start": v(33, 29) * mm, "end": v(41, 29) * mm});
            skLineSegment(sketch, "E18.10.3.2", {"start": v(33, 21) * mm, "end": v(41, 21) * mm});
            skLineSegment(sketch, "E18.10.3.3", {"start": v(33, 29) * mm, "end": v(33, 21) * mm});
            skLineSegment(sketch, "E18.10.4.0", {"start": v(41, 18) * mm, "end": v(41, 10) * mm});
            skLineSegment(sketch, "E18.10.4.1", {"start": v(33, 18) * mm, "end": v(41, 18) * mm});
            skLineSegment(sketch, "E18.10.4.2", {"start": v(33, 10) * mm, "end": v(41, 10) * mm});
            skLineSegment(sketch, "E18.10.4.3", {"start": v(33, 18) * mm, "end": v(33, 10) * mm});
            skLineSegment(sketch, "E18.10.5.0", {"start": v(41, 7) * mm, "end": v(41, -1) * mm});
            skLineSegment(sketch, "E18.10.5.1", {"start": v(33, 7) * mm, "end": v(41, 7) * mm});
            skLineSegment(sketch, "E18.10.5.2", {"start": v(33, -1) * mm, "end": v(41, -1) * mm});
            skLineSegment(sketch, "E18.10.5.3", {"start": v(33, 7) * mm, "end": v(33, -1) * mm});
            skLineSegment(sketch, "E18.10.6.0", {"start": v(41, -4) * mm, "end": v(41, -12) * mm});
            skLineSegment(sketch, "E18.10.6.1", {"start": v(33, -4) * mm, "end": v(41, -4) * mm});
            skLineSegment(sketch, "E18.10.6.2", {"start": v(33, -12) * mm, "end": v(41, -12) * mm});
            skLineSegment(sketch, "E18.10.6.3", {"start": v(33, -4) * mm, "end": v(33, -12) * mm});
            skLineSegment(sketch, "E18.10.7.0", {"start": v(41, -15) * mm, "end": v(41, -23) * mm});
            skLineSegment(sketch, "E18.10.7.1", {"start": v(33, -15) * mm, "end": v(41, -15) * mm});
            skLineSegment(sketch, "E18.10.7.2", {"start": v(33, -23) * mm, "end": v(41, -23) * mm});
            skLineSegment(sketch, "E18.10.7.3", {"start": v(33, -15) * mm, "end": v(33, -23) * mm});
            skLineSegment(sketch, "E18.10.8.0", {"start": v(41, -26) * mm, "end": v(41, -34) * mm});
            skLineSegment(sketch, "E18.10.8.1", {"start": v(33, -26) * mm, "end": v(41, -26) * mm});
            skLineSegment(sketch, "E18.10.8.2", {"start": v(33, -34) * mm, "end": v(41, -34) * mm});
            skLineSegment(sketch, "E18.10.8.3", {"start": v(33, -26) * mm, "end": v(33, -34) * mm});
            skLineSegment(sketch, "E18.10.9.0", {"start": v(41, -37) * mm, "end": v(41, -45) * mm});
            skLineSegment(sketch, "E18.10.9.1", {"start": v(33, -37) * mm, "end": v(41, -37) * mm});
            skLineSegment(sketch, "E18.10.9.2", {"start": v(33, -45) * mm, "end": v(41, -45) * mm});
            skLineSegment(sketch, "E18.10.9.3", {"start": v(33, -37) * mm, "end": v(33, -45) * mm});
            skLineSegment(sketch, "E18.10.10.0", {"start": v(41, -48) * mm, "end": v(41, -56) * mm});
            skLineSegment(sketch, "E18.10.10.1", {"start": v(33, -48) * mm, "end": v(41, -48) * mm});
            skLineSegment(sketch, "E18.10.10.2", {"start": v(33, -56) * mm, "end": v(41, -56) * mm});
            skLineSegment(sketch, "E18.10.10.3", {"start": v(33, -48) * mm, "end": v(33, -56) * mm});
            skLineSegment(sketch, "E18.11.0.0", {"start": v(52, 62) * mm, "end": v(52, 54) * mm});
            skLineSegment(sketch, "E18.11.0.1", {"start": v(44, 62) * mm, "end": v(52, 62) * mm});
            skLineSegment(sketch, "E18.11.0.2", {"start": v(44, 54) * mm, "end": v(52, 54) * mm});
            skLineSegment(sketch, "E18.11.0.3", {"start": v(44, 62) * mm, "end": v(44, 54) * mm});
            skLineSegment(sketch, "E18.11.1.0", {"start": v(52, 51) * mm, "end": v(52, 43) * mm});
            skLineSegment(sketch, "E18.11.1.1", {"start": v(44, 51) * mm, "end": v(52, 51) * mm});
            skLineSegment(sketch, "E18.11.1.2", {"start": v(44, 43) * mm, "end": v(52, 43) * mm});
            skLineSegment(sketch, "E18.11.1.3", {"start": v(44, 51) * mm, "end": v(44, 43) * mm});
            skLineSegment(sketch, "E18.11.2.0", {"start": v(52, 40) * mm, "end": v(52, 32) * mm});
            skLineSegment(sketch, "E18.11.2.1", {"start": v(44, 40) * mm, "end": v(52, 40) * mm});
            skLineSegment(sketch, "E18.11.2.2", {"start": v(44, 32) * mm, "end": v(52, 32) * mm});
            skLineSegment(sketch, "E18.11.2.3", {"start": v(44, 40) * mm, "end": v(44, 32) * mm});
            skLineSegment(sketch, "E18.11.3.0", {"start": v(52, 29) * mm, "end": v(52, 21) * mm});
            skLineSegment(sketch, "E18.11.3.1", {"start": v(44, 29) * mm, "end": v(52, 29) * mm});
            skLineSegment(sketch, "E18.11.3.2", {"start": v(44, 21) * mm, "end": v(52, 21) * mm});
            skLineSegment(sketch, "E18.11.3.3", {"start": v(44, 29) * mm, "end": v(44, 21) * mm});
            skLineSegment(sketch, "E18.11.4.0", {"start": v(52, 18) * mm, "end": v(52, 10) * mm});
            skLineSegment(sketch, "E18.11.4.1", {"start": v(44, 18) * mm, "end": v(52, 18) * mm});
            skLineSegment(sketch, "E18.11.4.2", {"start": v(44, 10) * mm, "end": v(52, 10) * mm});
            skLineSegment(sketch, "E18.11.4.3", {"start": v(44, 18) * mm, "end": v(44, 10) * mm});
            skLineSegment(sketch, "E18.11.5.0", {"start": v(52, 7) * mm, "end": v(52, -1) * mm});
            skLineSegment(sketch, "E18.11.5.1", {"start": v(44, 7) * mm, "end": v(52, 7) * mm});
            skLineSegment(sketch, "E18.11.5.2", {"start": v(44, -1) * mm, "end": v(52, -1) * mm});
            skLineSegment(sketch, "E18.11.5.3", {"start": v(44, 7) * mm, "end": v(44, -1) * mm});
            skLineSegment(sketch, "E18.11.6.0", {"start": v(52, -4) * mm, "end": v(52, -12) * mm});
            skLineSegment(sketch, "E18.11.6.1", {"start": v(44, -4) * mm, "end": v(52, -4) * mm});
            skLineSegment(sketch, "E18.11.6.2", {"start": v(44, -12) * mm, "end": v(52, -12) * mm});
            skLineSegment(sketch, "E18.11.6.3", {"start": v(44, -4) * mm, "end": v(44, -12) * mm});
            skLineSegment(sketch, "E18.11.7.0", {"start": v(52, -15) * mm, "end": v(52, -23) * mm});
            skLineSegment(sketch, "E18.11.7.1", {"start": v(44, -15) * mm, "end": v(52, -15) * mm});
            skLineSegment(sketch, "E18.11.7.2", {"start": v(44, -23) * mm, "end": v(52, -23) * mm});
            skLineSegment(sketch, "E18.11.7.3", {"start": v(44, -15) * mm, "end": v(44, -23) * mm});
            skLineSegment(sketch, "E18.11.8.0", {"start": v(52, -26) * mm, "end": v(52, -34) * mm});
            skLineSegment(sketch, "E18.11.8.1", {"start": v(44, -26) * mm, "end": v(52, -26) * mm});
            skLineSegment(sketch, "E18.11.8.2", {"start": v(44, -34) * mm, "end": v(52, -34) * mm});
            skLineSegment(sketch, "E18.11.8.3", {"start": v(44, -26) * mm, "end": v(44, -34) * mm});
            skLineSegment(sketch, "E18.11.9.0", {"start": v(52, -37) * mm, "end": v(52, -45) * mm});
            skLineSegment(sketch, "E18.11.9.1", {"start": v(44, -37) * mm, "end": v(52, -37) * mm});
            skLineSegment(sketch, "E18.11.9.2", {"start": v(44, -45) * mm, "end": v(52, -45) * mm});
            skLineSegment(sketch, "E18.11.9.3", {"start": v(44, -37) * mm, "end": v(44, -45) * mm});
            skLineSegment(sketch, "E18.11.10.0", {"start": v(52, -48) * mm, "end": v(52, -56) * mm});
            skLineSegment(sketch, "E18.11.10.1", {"start": v(44, -48) * mm, "end": v(52, -48) * mm});
            skLineSegment(sketch, "E18.11.10.2", {"start": v(44, -56) * mm, "end": v(52, -56) * mm});
            skLineSegment(sketch, "E18.11.10.3", {"start": v(44, -48) * mm, "end": v(44, -56) * mm});
            skLineSegment(sketch, "E18.12.0.0", {"start": v(63, 62) * mm, "end": v(63, 54) * mm});
            skLineSegment(sketch, "E18.12.0.1", {"start": v(55, 62) * mm, "end": v(63, 62) * mm});
            skLineSegment(sketch, "E18.12.0.2", {"start": v(55, 54) * mm, "end": v(63, 54) * mm});
            skLineSegment(sketch, "E18.12.0.3", {"start": v(55, 62) * mm, "end": v(55, 54) * mm});
            skLineSegment(sketch, "E18.12.1.0", {"start": v(63, 51) * mm, "end": v(63, 43) * mm});
            skLineSegment(sketch, "E18.12.1.1", {"start": v(55, 51) * mm, "end": v(63, 51) * mm});
            skLineSegment(sketch, "E18.12.1.2", {"start": v(55, 43) * mm, "end": v(63, 43) * mm});
            skLineSegment(sketch, "E18.12.1.3", {"start": v(55, 51) * mm, "end": v(55, 43) * mm});
            skLineSegment(sketch, "E18.12.2.0", {"start": v(63, 40) * mm, "end": v(63, 32) * mm});
            skLineSegment(sketch, "E18.12.2.1", {"start": v(55, 40) * mm, "end": v(63, 40) * mm});
            skLineSegment(sketch, "E18.12.2.2", {"start": v(55, 32) * mm, "end": v(63, 32) * mm});
            skLineSegment(sketch, "E18.12.2.3", {"start": v(55, 40) * mm, "end": v(55, 32) * mm});
            skLineSegment(sketch, "E18.12.3.0", {"start": v(63, 29) * mm, "end": v(63, 21) * mm});
            skLineSegment(sketch, "E18.12.3.1", {"start": v(55, 29) * mm, "end": v(63, 29) * mm});
            skLineSegment(sketch, "E18.12.3.2", {"start": v(55, 21) * mm, "end": v(63, 21) * mm});
            skLineSegment(sketch, "E18.12.3.3", {"start": v(55, 29) * mm, "end": v(55, 21) * mm});
            skLineSegment(sketch, "E18.12.4.0", {"start": v(63, 18) * mm, "end": v(63, 10) * mm});
            skLineSegment(sketch, "E18.12.4.1", {"start": v(55, 18) * mm, "end": v(63, 18) * mm});
            skLineSegment(sketch, "E18.12.4.2", {"start": v(55, 10) * mm, "end": v(63, 10) * mm});
            skLineSegment(sketch, "E18.12.4.3", {"start": v(55, 18) * mm, "end": v(55, 10) * mm});
            skLineSegment(sketch, "E18.12.5.0", {"start": v(63, 7) * mm, "end": v(63, -1) * mm});
            skLineSegment(sketch, "E18.12.5.1", {"start": v(55, 7) * mm, "end": v(63, 7) * mm});
            skLineSegment(sketch, "E18.12.5.2", {"start": v(55, -1) * mm, "end": v(63, -1) * mm});
            skLineSegment(sketch, "E18.12.5.3", {"start": v(55, 7) * mm, "end": v(55, -1) * mm});
            skLineSegment(sketch, "E18.12.6.0", {"start": v(63, -4) * mm, "end": v(63, -12) * mm});
            skLineSegment(sketch, "E18.12.6.1", {"start": v(55, -4) * mm, "end": v(63, -4) * mm});
            skLineSegment(sketch, "E18.12.6.2", {"start": v(55, -12) * mm, "end": v(63, -12) * mm});
            skLineSegment(sketch, "E18.12.6.3", {"start": v(55, -4) * mm, "end": v(55, -12) * mm});
            skLineSegment(sketch, "E18.12.7.0", {"start": v(63, -15) * mm, "end": v(63, -23) * mm});
            skLineSegment(sketch, "E18.12.7.1", {"start": v(55, -15) * mm, "end": v(63, -15) * mm});
            skLineSegment(sketch, "E18.12.7.2", {"start": v(55, -23) * mm, "end": v(63, -23) * mm});
            skLineSegment(sketch, "E18.12.7.3", {"start": v(55, -15) * mm, "end": v(55, -23) * mm});
            skLineSegment(sketch, "E18.12.8.0", {"start": v(63, -26) * mm, "end": v(63, -34) * mm});
            skLineSegment(sketch, "E18.12.8.1", {"start": v(55, -26) * mm, "end": v(63, -26) * mm});
            skLineSegment(sketch, "E18.12.8.2", {"start": v(55, -34) * mm, "end": v(63, -34) * mm});
            skLineSegment(sketch, "E18.12.8.3", {"start": v(55, -26) * mm, "end": v(55, -34) * mm});
            skLineSegment(sketch, "E18.12.9.0", {"start": v(63, -37) * mm, "end": v(63, -45) * mm});
            skLineSegment(sketch, "E18.12.9.1", {"start": v(55, -37) * mm, "end": v(63, -37) * mm});
            skLineSegment(sketch, "E18.12.9.2", {"start": v(55, -45) * mm, "end": v(63, -45) * mm});
            skLineSegment(sketch, "E18.12.9.3", {"start": v(55, -37) * mm, "end": v(55, -45) * mm});
            skLineSegment(sketch, "E18.12.10.0", {"start": v(63, -48) * mm, "end": v(63, -56) * mm});
            skLineSegment(sketch, "E18.12.10.1", {"start": v(55, -48) * mm, "end": v(63, -48) * mm});
            skLineSegment(sketch, "E18.12.10.2", {"start": v(55, -56) * mm, "end": v(63, -56) * mm});
            skLineSegment(sketch, "E18.12.10.3", {"start": v(55, -48) * mm, "end": v(55, -56) * mm});
            skLineSegment(sketch, "E18.13.0.0", {"start": v(74, 62) * mm, "end": v(74, 54) * mm});
            skLineSegment(sketch, "E18.13.0.1", {"start": v(66, 62) * mm, "end": v(74, 62) * mm});
            skLineSegment(sketch, "E18.13.0.2", {"start": v(66, 54) * mm, "end": v(74, 54) * mm});
            skLineSegment(sketch, "E18.13.0.3", {"start": v(66, 62) * mm, "end": v(66, 54) * mm});
            skLineSegment(sketch, "E18.13.1.0", {"start": v(74, 51) * mm, "end": v(74, 43) * mm});
            skLineSegment(sketch, "E18.13.1.1", {"start": v(66, 51) * mm, "end": v(74, 51) * mm});
            skLineSegment(sketch, "E18.13.1.2", {"start": v(66, 43) * mm, "end": v(74, 43) * mm});
            skLineSegment(sketch, "E18.13.1.3", {"start": v(66, 51) * mm, "end": v(66, 43) * mm});
            skLineSegment(sketch, "E18.13.2.0", {"start": v(74, 40) * mm, "end": v(74, 32) * mm});
            skLineSegment(sketch, "E18.13.2.1", {"start": v(66, 40) * mm, "end": v(74, 40) * mm});
            skLineSegment(sketch, "E18.13.2.2", {"start": v(66, 32) * mm, "end": v(74, 32) * mm});
            skLineSegment(sketch, "E18.13.2.3", {"start": v(66, 40) * mm, "end": v(66, 32) * mm});
            skLineSegment(sketch, "E18.13.3.0", {"start": v(74, 29) * mm, "end": v(74, 21) * mm});
            skLineSegment(sketch, "E18.13.3.1", {"start": v(66, 29) * mm, "end": v(74, 29) * mm});
            skLineSegment(sketch, "E18.13.3.2", {"start": v(66, 21) * mm, "end": v(74, 21) * mm});
            skLineSegment(sketch, "E18.13.3.3", {"start": v(66, 29) * mm, "end": v(66, 21) * mm});
            skLineSegment(sketch, "E18.13.4.0", {"start": v(74, 18) * mm, "end": v(74, 10) * mm});
            skLineSegment(sketch, "E18.13.4.1", {"start": v(66, 18) * mm, "end": v(74, 18) * mm});
            skLineSegment(sketch, "E18.13.4.2", {"start": v(66, 10) * mm, "end": v(74, 10) * mm});
            skLineSegment(sketch, "E18.13.4.3", {"start": v(66, 18) * mm, "end": v(66, 10) * mm});
            skLineSegment(sketch, "E18.13.5.0", {"start": v(74, 7) * mm, "end": v(74, -1) * mm});
            skLineSegment(sketch, "E18.13.5.1", {"start": v(66, 7) * mm, "end": v(74, 7) * mm});
            skLineSegment(sketch, "E18.13.5.2", {"start": v(66, -1) * mm, "end": v(74, -1) * mm});
            skLineSegment(sketch, "E18.13.5.3", {"start": v(66, 7) * mm, "end": v(66, -1) * mm});
            skLineSegment(sketch, "E18.13.6.0", {"start": v(74, -4) * mm, "end": v(74, -12) * mm});
            skLineSegment(sketch, "E18.13.6.1", {"start": v(66, -4) * mm, "end": v(74, -4) * mm});
            skLineSegment(sketch, "E18.13.6.2", {"start": v(66, -12) * mm, "end": v(74, -12) * mm});
            skLineSegment(sketch, "E18.13.6.3", {"start": v(66, -4) * mm, "end": v(66, -12) * mm});
            skLineSegment(sketch, "E18.13.7.0", {"start": v(74, -15) * mm, "end": v(74, -23) * mm});
            skLineSegment(sketch, "E18.13.7.1", {"start": v(66, -15) * mm, "end": v(74, -15) * mm});
            skLineSegment(sketch, "E18.13.7.2", {"start": v(66, -23) * mm, "end": v(74, -23) * mm});
            skLineSegment(sketch, "E18.13.7.3", {"start": v(66, -15) * mm, "end": v(66, -23) * mm});
            skLineSegment(sketch, "E18.13.8.0", {"start": v(74, -26) * mm, "end": v(74, -34) * mm});
            skLineSegment(sketch, "E18.13.8.1", {"start": v(66, -26) * mm, "end": v(74, -26) * mm});
            skLineSegment(sketch, "E18.13.8.2", {"start": v(66, -34) * mm, "end": v(74, -34) * mm});
            skLineSegment(sketch, "E18.13.8.3", {"start": v(66, -26) * mm, "end": v(66, -34) * mm});
            skLineSegment(sketch, "E18.13.9.0", {"start": v(74, -37) * mm, "end": v(74, -45) * mm});
            skLineSegment(sketch, "E18.13.9.1", {"start": v(66, -37) * mm, "end": v(74, -37) * mm});
            skLineSegment(sketch, "E18.13.9.2", {"start": v(66, -45) * mm, "end": v(74, -45) * mm});
            skLineSegment(sketch, "E18.13.9.3", {"start": v(66, -37) * mm, "end": v(66, -45) * mm});
            skLineSegment(sketch, "E18.13.10.0", {"start": v(74, -48) * mm, "end": v(74, -56) * mm});
            skLineSegment(sketch, "E18.13.10.1", {"start": v(66, -48) * mm, "end": v(74, -48) * mm});
            skLineSegment(sketch, "E18.13.10.2", {"start": v(66, -56) * mm, "end": v(74, -56) * mm});
            skLineSegment(sketch, "E18.13.10.3", {"start": v(66, -48) * mm, "end": v(66, -56) * mm});
            skLineSegment(sketch, "E18.direction1", {"start": v(-77, 54) * mm, "end": v(-66, 54) * mm, "construction": true});
            skLineSegment(sketch, "E18.direction2", {"start": v(-77, 54) * mm, "end": v(-77, 43) * mm, "construction": true});
            skSolve(sketch);
        }
        {
            var Q0;
            Q0 = qSketchRegion(id + "F4", true);
            extrude(context, id + "F5", {"entities" : qUnion([Q0]), "operationType" : NewBodyOperationType.REMOVE, "oppositeDirection" : true, "depth" : 170 * mm, "offsetDistance" : 25 * mm});
        }
        {
            var Q0;
            Q0 = qSketchRegion(id + "F4", true);
            extrude(context, id + "F7", {"entities" : qUnion([Q0]), "operationType" : NewBodyOperationType.REMOVE, "oppositeDirection" : true, "depth" : 3 * mm, "offsetDistance" : 25 * mm});
        }
    });
